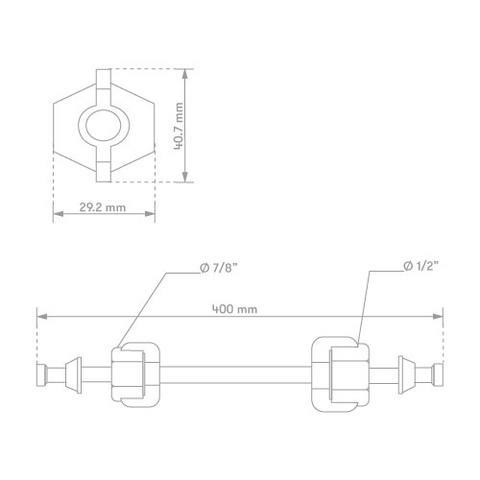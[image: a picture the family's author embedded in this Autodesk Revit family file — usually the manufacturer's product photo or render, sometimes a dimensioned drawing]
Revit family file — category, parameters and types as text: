
# Revit family: BIM_01-1921-00
name_source: partatom
category: Plumbing Fixtures
units: mm (PartAtom-declared; Revit-internal decimal feet)

## family parameters
Classification Number = 23.31.11.00
Cut with Voids When Loaded = No
Enable Cutting in Views = No
Host = Face
Maintain Annotation Orientation = No
Part Type = Normal
Room Calculation Point = No
Round Connector Dimension = Use Diameter
Shared = No

## types (1)
- 01-1921-00
    CW Connection = Yes
    Conexiones = Acometida: Rosca hembra ½” NPT.
Válvula: Rosca hembra 15/16” x 14 hilos UNS
    Date Modified = 22/08/2025
    Default Elevation = 0 mm  [stored 0 ft]
    Description = Accesorio
    Diametro = 12.7 mm  [stored 0.0416667 ft]
    Diametro nominal = 5,5 mm
    Empaque-Alto = 40.7 mm  [stored 0.13353 ft]
    Empaque-Ancho = 29.2 mm
    Empaque-Profundidad = 27.3 mm
    Garantia Especifica = 20 AÑOS
    HW Connection = Yes
    Largo = 400 mm  [stored 1.31234 ft]
    Link Ficha Tecnica = https://infotecnica.gricol.com
    Manufacturer = Gricol
    Materiales del producto = Polietileno, Polipropileno, Caucho
    Model = 01-1921-00
    Plastico = Plástico
    Plastico - ABS + Colorante azul = Plastico - ABS + Colorante azul
    Presión Maxima = 125.00 psi
    Presión Mínima = 20.00 psi
    Presión de Estallído = 250.00 psi
    Product Name = Conector Sanitario
    Referente Normativo = NTC 5441, ASME A112.18.6 / CSA B125.6
    Resistencia a Corrosión = NTC 1156 Sal Neutral
    Sitio web = https://www.gricol.com
    Temperaturas de trabajo = DE 5° A 71°
    Tipo de Uso = Domestico
    Type Image = CONECTOR SANITARIO H ½” x H 7-8”.jpg
    URL = https://www.gricol.com
    Vent Connection = No
    Vida Util = 100000 CICLOS
    Waste Connection = No

note: [stored X ft] marks values corroborated as IEEE doubles in the binary element streams (Revit-internal decimal feet)

## geometry (parser evidence)
native form markers: Blend x8, Sweep x3
no freeform markers — native parametric forms only
